# Revit family: IS_Contour21_S5059_BIM_DE
name_source: partatom
category: Plumbing Fixtures
revit_build: Autodesk Revit MEP 2016 (Build: 20161004_0715(x64)
units: mm (PartAtom-declared; Revit-internal decimal feet)

## family parameters
Always vertical = No
Cut with Voids When Loaded = No
OmniClass Number = 23.45.05.14.17.11
OmniClass Title = Shower Compartments
Part Type = Normal
Room Calculation Point = No
Round Connector Dimension = Use Diameter
Shared = No
Work Plane-Based = No

## types (1)
- S5059BH - IS Spiegel CONNECT FREEDOM, justierbar
    Accessories = www.idealstandard.de\ersatzteile
    Assembly Code = C1030200
    AssetType = Fest
    BIMobject category = Mirrors
    BOSUseNativeGeometries = 1
    BarCode = 5017830425526
    Brand = Ideal Standard
    Brand url = http://www.idealstandard.de
    Color = Mirrored
    Cost = 0 $
    CurrencyUnit = €
    CurrentRevision = 1
    Date of publishing = 15/09/2017
    Description = S5059BH CONNECT FREEDOM mirror
    DurationUnit = Jahr
    EAN code = https://5017830425526
    Edition number = 1
    ExpectedLife = 25
    Features = CONNECT FREEDOM mirror
    Finish = Mirrored
    IFC Classification = Sanitary Terminal
    Installation instructions = http://www.idealstandard.de
    InstallationInstructions = www.idealstandard.de\produkte
    MainColor = Mirrored
    Manufacturer = www.idealstandard.de\produkte
    Manufacturer name = Ideal Standard
    ManufacturerURL = http://www.idealstandard.de
    Material main = Glass
    Model = S5059BH
    ModelNumber = S5059BH
    ModelReference = S5059BH CONNECT FREEDOM mirror
    NettWeight = 6,95 kg
    Nominal height = 0
    Nominal width = 0
    NominalHeight = 700 mm
    NominalLength = 90 mm
    NominalWidth = 500 mm
    Product Guid = 7fb75c2f-1a99-489e-8eb3-cefff4330cc3
    Product SKU = S5059
    Product data url = https://bimobject.com
    Product family = CONTOUR 21
    Product group = Mirror
    Product name = CONNECT FREEDOM mirror
    Product url = http://www.idealstandard.de
    ProductInformation = www.idealstandard.de\produkte
    QR code = http://bimobject.com
    Shape = Sculptured
    Size = 700 x 90 x 500mm
    Space = Intern
    SpareParts = www.idealstandard.de/ersatzteile
    Technical description = http://www.idealstandard.de
    URL = http://www.idealstandard.de
    Uniclass2015Code = Pr_25_71_53_06
    Uniclass2015Title = Bathroom mirrors
    Uniclass2015Version = Products v1.1
    Version = 1
    VolumeUnits = Litres
    Weight Net (Kg) = 6.95

## geometry (parser evidence)
native form markers: Blend x4, Sweep x1
no freeform markers — native parametric forms only
